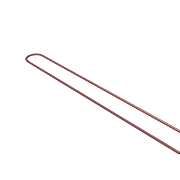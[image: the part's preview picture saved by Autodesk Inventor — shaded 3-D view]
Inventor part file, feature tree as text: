
AUTODESK INVENTOR PART (.ipt)
format: ipt  version: unknown  size: 159,232 bytes
history: native  units: mm
features: sketch x2, sweep x1
ambient origin geometry x8: Origin, YZ Plane, XZ Plane, XY Plane, X Axis, Y Axis, Z Axis, Center Point
feature tree (3):
  sweep  "Sweep1"
  sketch  "Sketch1"  dims[d0=190.0mm d1=20.0mm]
  sketch  "Sketch2"  dims[d2=10.0mm d3=2.0mm d4=0.0mm]
